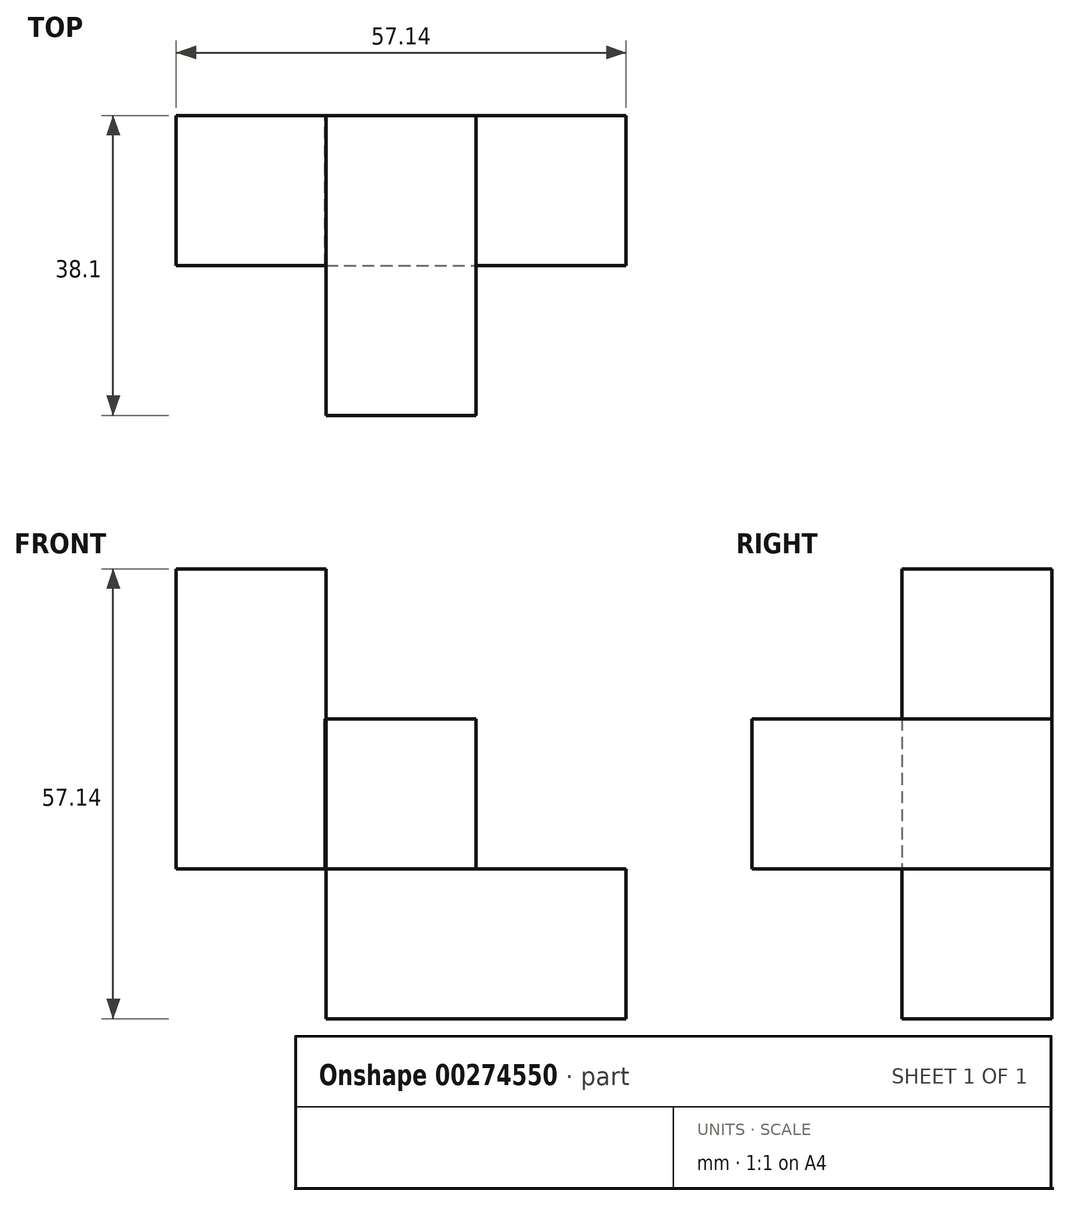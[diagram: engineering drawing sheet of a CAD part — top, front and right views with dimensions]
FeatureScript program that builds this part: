
annotation { "Feature Type Name" : "Feature", "Feature Type Description" : "" }
export const myFeature = defineFeature(function(context is Context, id is Id, definition is map)
    precondition{}
    {
        {
            var Q0;
            Q0=qCreatedBy(makeId("Front.planeOp"),FACE);
            var sketch = newSketch(context, id + "F0", { "sketchPlane" : qUnion([Q0])});
            skLineSegment(sketch, "E0.bottom", {"start": v(-9.53, 9.52) * mm, "end": v(9.53, 9.52) * mm});
            skLineSegment(sketch, "E0.top", {"start": v(-9.53, -9.52) * mm, "end": v(9.53, -9.52) * mm});
            skLineSegment(sketch, "E0.left", {"start": v(-9.52, 9.52) * mm, "end": v(-9.52, -9.52) * mm});
            skLineSegment(sketch, "E0.right", {"start": v(9.52, 9.52) * mm, "end": v(9.52, -9.52) * mm});
            skLineSegment(sketch, "E1.bottom", {"start": v(-28.57, 9.52) * mm, "end": v(-9.68, 9.52) * mm});
            skLineSegment(sketch, "E1.top", {"start": v(-28.57, -9.52) * mm, "end": v(-9.68, -9.52) * mm});
            skLineSegment(sketch, "E1.left", {"start": v(-28.58, 9.52) * mm, "end": v(-28.58, -9.53) * mm});
            skLineSegment(sketch, "E1.right", {"start": v(-9.68, 9.52) * mm, "end": v(-9.68, -9.52) * mm});
            skPoint(sketch, "E1.middle", {"position": v(-19.13, 0) * mm});
            skLineSegment(sketch, "E2.bottom", {"start": v(-28.57, 28.58) * mm, "end": v(-9.53, 28.58) * mm});
            skLineSegment(sketch, "E2.top", {"start": v(-28.57, 9.52) * mm, "end": v(-9.53, 9.52) * mm});
            skLineSegment(sketch, "E2.left", {"start": v(-28.58, 28.58) * mm, "end": v(-28.58, 9.52) * mm});
            skLineSegment(sketch, "E2.right", {"start": v(-9.53, 28.58) * mm, "end": v(-9.53, 9.52) * mm});
            skPoint(sketch, "E2.middle", {"position": v(-19.05, 19.05) * mm});
            skLineSegment(sketch, "E3.bottom", {"start": v(-9.53, -9.52) * mm, "end": v(9.52, -9.52) * mm});
            skLineSegment(sketch, "E3.top", {"start": v(-9.53, -28.58) * mm, "end": v(9.52, -28.58) * mm});
            skLineSegment(sketch, "E3.left", {"start": v(-9.52, -9.52) * mm, "end": v(-9.52, -28.58) * mm});
            skLineSegment(sketch, "E3.right", {"start": v(9.52, -9.52) * mm, "end": v(9.52, -28.58) * mm});
            skPoint(sketch, "E3.middle", {"position": v(0, -19.05) * mm});
            skLineSegment(sketch, "E4.bottom", {"start": v(9.53, -9.52) * mm, "end": v(28.57, -9.52) * mm});
            skLineSegment(sketch, "E4.top", {"start": v(9.53, -28.57) * mm, "end": v(28.57, -28.57) * mm});
            skLineSegment(sketch, "E4.left", {"start": v(9.52, -9.52) * mm, "end": v(9.52, -28.57) * mm});
            skLineSegment(sketch, "E4.right", {"start": v(28.57, -9.52) * mm, "end": v(28.57, -28.57) * mm});
            skPoint(sketch, "E4.middle", {"position": v(19.05, -19.05) * mm});
            skSolve(sketch);
        }
        {
            var Q0;
            Q0=makeQuery(id+"F0.imprint","IMPRINT",FACE,{"disambiguationData":[TD([[makeQuery(id+"F0.imprint","IMPRINT",EDGE,{"derivedFrom":sQuery(id+"F0.wireOp",EDGE,"E1.top")}),1.0]])]});
            var Q1;
            Q1=makeQuery(id+"F0.imprint","IMPRINT",FACE,{"disambiguationData":[TD([[makeQuery(id+"F0.imprint","IMPRINT",EDGE,{"derivedFrom":sQuery(id+"F0.wireOp",EDGE,"E4.bottom")}),-1.0]])]});
            var Q2;
            Q2=makeQuery(id+"F0.imprint","IMPRINT",FACE,{"disambiguationData":[TD([[makeQuery(id+"F0.imprint","IMPRINT",EDGE,{"derivedFrom":sQuery(id+"F0.wireOp",EDGE,"E3.bottom")}),-1.0]])]});
            var Q3;
            Q3=makeQuery(id+"F0.imprint","IMPRINT",FACE,{"disambiguationData":[TD([[makeQuery(id+"F0.imprint","IMPRINT",EDGE,{"derivedFrom":sQuery(id+"F0.wireOp",EDGE,"E2.bottom")}),-1.0]])]});
            extrude(context, id + "F1", {"entities" : qUnion([Q0, Q1, Q2, Q3]), "depth" : 19.05 * mm});
        }
        {
            var Q0;
            Q0=makeQuery(id+"F0.imprint","IMPRINT",FACE,{"disambiguationData":[TD([[makeQuery(id+"F0.imprint","IMPRINT",EDGE,{"derivedFrom":sQuery(id+"F0.wireOp",EDGE,"E0.bottom")}),-1.0]])]});
            extrude(context, id + "F2", {"entities" : qUnion([Q0]), "depth" : 38.1 * mm});
        }
    });
